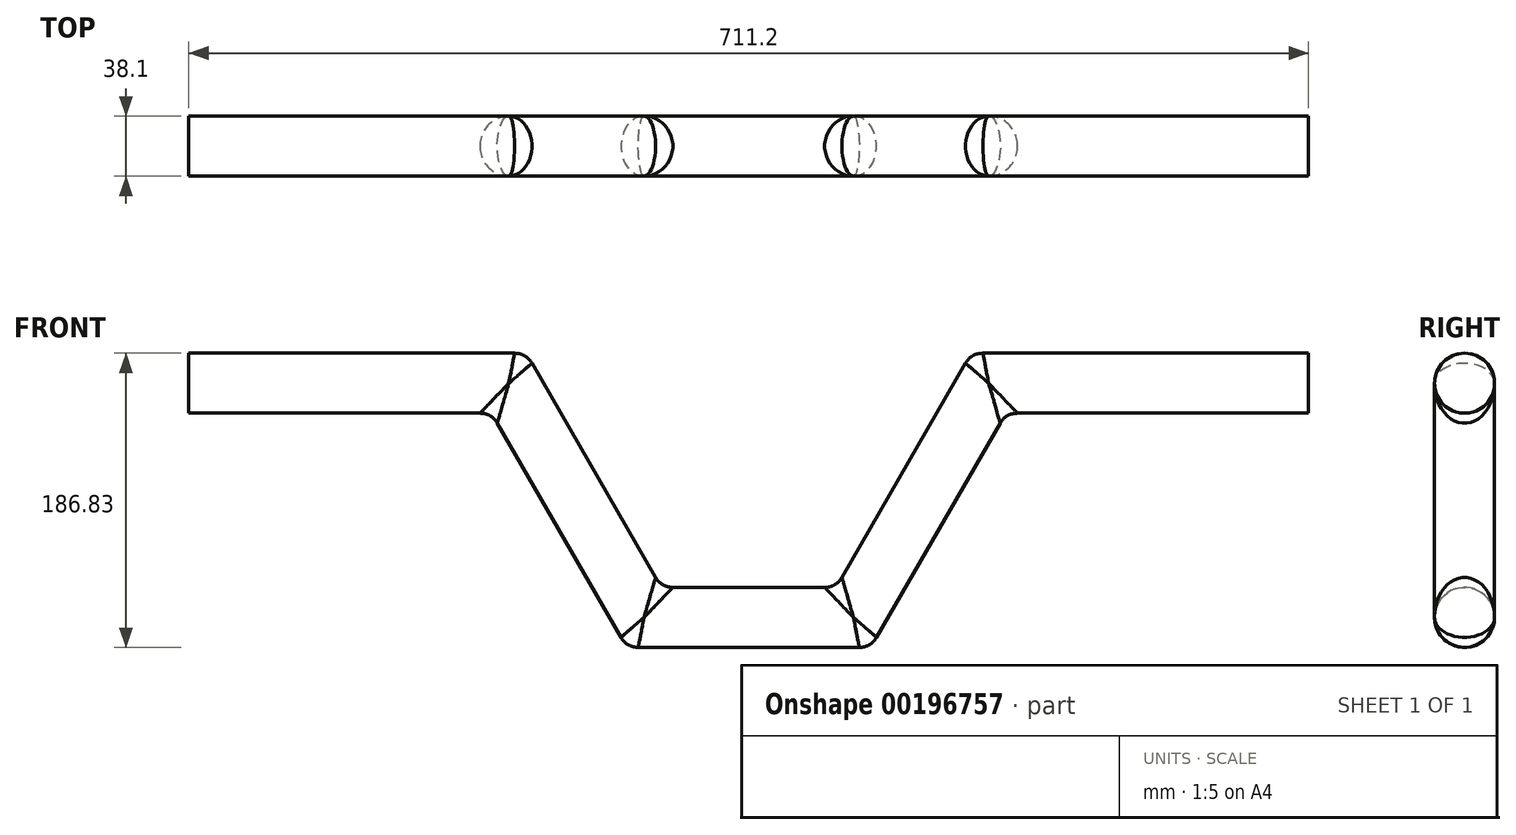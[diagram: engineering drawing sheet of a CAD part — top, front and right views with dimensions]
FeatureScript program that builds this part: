
annotation { "Feature Type Name" : "Feature", "Feature Type Description" : "" }
export const myFeature = defineFeature(function(context is Context, id is Id, definition is map)
    precondition{}
    {
        {
            var Q0;
            Q0=qCreatedBy(makeId("Right.planeOp"),FACE);
            var sketch = newSketch(context, id + "F0", { "sketchPlane" : qUnion([Q0])});
            skCircle(sketch, "E0", {"center": v(0, 0) * mm, "radius": 19.05 * mm});
            skSolve(sketch);
        }
        {
            var Q0;
            Q0=qCreatedBy(makeId("Front.planeOp"),FACE);
            var sketch = newSketch(context, id + "F1", { "sketchPlane" : qUnion([Q0])});
            skLineSegment(sketch, "E1", {"start": v(0, 0) * mm, "end": v(203.2, 0) * mm});
            skLineSegment(sketch, "E2", {"start": v(203.2, 0) * mm, "end": v(289.07, -148.73) * mm});
            skLineSegment(sketch, "E3", {"start": v(289.07, -148.73) * mm, "end": v(422.13, -148.73) * mm});
            skLineSegment(sketch, "E4", {"start": v(422.13, -148.73) * mm, "end": v(508, 0) * mm});
            skLineSegment(sketch, "E5", {"start": v(508, 0) * mm, "end": v(711.2, 0) * mm});
            skSolve(sketch);
        }
        {
            var Q0;
            Q0=makeQuery(id+"F0.imprint","IMPRINT",FACE,{"disambiguationData":[TD([[makeQuery(id+"F0.imprint","IMPRINT",EDGE,{"derivedFrom":sQuery(id+"F0.wireOp",EDGE,"E0")}),1.0]])]});
            var Q1;
            Q1=sQuery(id+"F1.wireOp",EDGE,"E1");
            var Q2;
            Q2=sQuery(id+"F1.wireOp",EDGE,"E2");
            var Q3;
            Q3=sQuery(id+"F1.wireOp",EDGE,"E3");
            var Q4;
            Q4=sQuery(id+"F1.wireOp",EDGE,"E4");
            var Q5;
            Q5=sQuery(id+"F1.wireOp",EDGE,"E5");
            sweep(context, id + "F2", {"profiles" : qUnion([Q0]), "path" : qUnion([Q1, Q2, Q3, Q4, Q5])});
        }
        {
            var Q0;
            Q0=makeQuery(id+"F2.opSweep","MID_CAP_EDGE",EDGE,{"disambiguationData":[OSD([sQuery(id+"F0.wireOp",EDGE,"E0"),sQuery(id+"F1.wireOp",VERTEX,"E2.start")])],"capPos":1.0});
            var Q1;
            Q1=makeQuery(id+"F2.opSweep","MID_CAP_EDGE",EDGE,{"disambiguationData":[OSD([sQuery(id+"F0.wireOp",EDGE,"E0"),sQuery(id+"F1.wireOp",VERTEX,"E3.start")])],"capPos":2.0});
            var Q2;
            Q2=makeQuery(id+"F2.opSweep","MID_CAP_EDGE",EDGE,{"disambiguationData":[OSD([sQuery(id+"F0.wireOp",EDGE,"E0"),sQuery(id+"F1.wireOp",VERTEX,"E4.start")])],"capPos":3.0});
            var Q3;
            Q3=makeQuery(id+"F2.opSweep","MID_CAP_EDGE",EDGE,{"disambiguationData":[OSD([sQuery(id+"F0.wireOp",EDGE,"E0"),sQuery(id+"F1.wireOp",VERTEX,"E5.start")])],"capPos":4.0});
            fillet(context, id + "F3", {"entities" : qUnion([Q0, Q1, Q2, Q3]), "radius" : 12.7 * mm, "rho" : 0.5, "crossSection" : FilletCrossSection.CONIC, "allowEdgeOverflow" : false});
        }
    });
